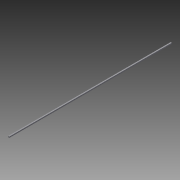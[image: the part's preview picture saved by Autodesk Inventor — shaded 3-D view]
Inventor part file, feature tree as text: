
AUTODESK INVENTOR PART (.ipt)
format: ipt  version: 2014 (Build 180170000, 170)  size: 67,584 bytes
history: native  units: in
note: dims shown in document units (in); Inventor stores cm internally (conversion verified against a paired STEP export)
features: extrude x1, sketch x1
ambient origin geometry x8: Origin, YZ Plane, XZ Plane, XY Plane, X Axis, Y Axis, Z Axis, Center Point
bodies: Solid1 (feature_tree)
feature tree (2):
  extrude  "Extrusion1"  Depth=0.25in
  sketch  "Sketch1"  dims[d0=36.0in d1=0.25in d2=0.25in d3=0.0in]
